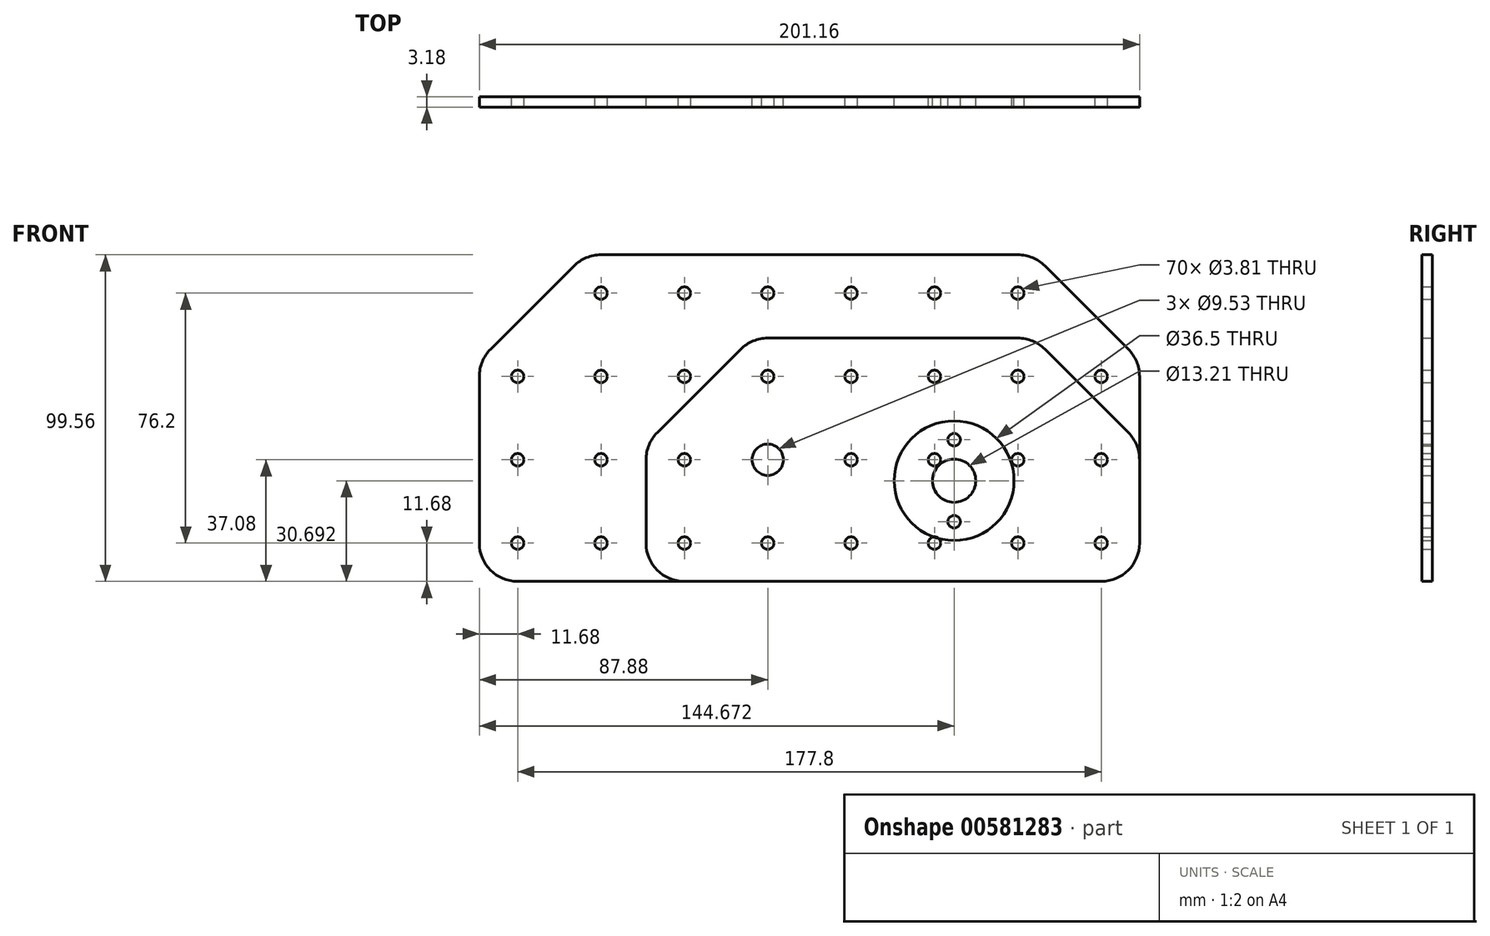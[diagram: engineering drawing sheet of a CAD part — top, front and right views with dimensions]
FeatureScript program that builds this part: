
annotation { "Feature Type Name" : "Feature", "Feature Type Description" : "" }
export const myFeature = defineFeature(function(context is Context, id is Id, definition is map)
    precondition{}
    {
        {
            var Q0;
            Q0=qCreatedBy(makeId("Front.planeOp"),FACE);
            var sketch = newSketch(context, id + "F0", { "sketchPlane" : qUnion([Q0])});
            skCircle(sketch, "E0", {"center": v(0, 0) * mm, "radius": 4.76 * mm});
            skCircle(sketch, "E1", {"center": v(0, 0) * mm, "radius": 50.8 * mm, "construction": true});
            skCircle(sketch, "E2", {"center": v(0, 0) * mm, "radius": 25.4 * mm, "construction": true});
            skCircle(sketch, "E3", {"center": v(56.8, -6.39) * mm, "radius": 6.6 * mm});
            skCircle(sketch, "E4", {"center": v(56.8, -6.39) * mm, "radius": 6.35 * mm, "construction": true});
            skCircle(sketch, "E5", {"center": v(56.8, -18.88) * mm, "radius": 1.9 * mm});
            skCircle(sketch, "E6", {"center": v(56.8, 6.1) * mm, "radius": 1.9 * mm});
            skLineSegment(sketch, "E7", {"start": v(56.8, -18.88) * mm, "end": v(56.8, 6.1) * mm, "construction": true});
            skCircle(sketch, "E8", {"center": v(56.8, -6.39) * mm, "radius": 18 * mm, "construction": true});
            skLineSegment(sketch, "E9", {"start": v(-87.88, -37.08) * mm, "end": v(113.28, -37.08) * mm});
            skCircle(sketch, "E10", {"center": v(0, 0) * mm, "radius": 6.35 * mm, "construction": true});
            skPoint(sketch, "E11", {"position": v(12.7, -37.08) * mm});
            skCircle(sketch, "E12", {"center": v(101.6, -25.4) * mm, "radius": 1.9 * mm});
            skCircle(sketch, "E13.0.1.0", {"center": v(101.6, 0) * mm, "radius": 1.9 * mm});
            skCircle(sketch, "E13.0.2.0", {"center": v(101.6, 25.4) * mm, "radius": 1.9 * mm});
            skCircle(sketch, "E13.0.3.0", {"center": v(101.6, 50.8) * mm, "radius": 1.9 * mm, "construction": true});
            skCircle(sketch, "E13.1.0.0", {"center": v(76.2, -25.4) * mm, "radius": 1.9 * mm});
            skCircle(sketch, "E13.1.1.0", {"center": v(76.2, 0) * mm, "radius": 1.9 * mm});
            skCircle(sketch, "E13.1.2.0", {"center": v(76.2, 25.4) * mm, "radius": 1.9 * mm});
            skCircle(sketch, "E13.1.3.0", {"center": v(76.2, 50.8) * mm, "radius": 1.9 * mm});
            skCircle(sketch, "E13.2.0.0", {"center": v(50.8, -25.4) * mm, "radius": 1.9 * mm, "construction": true});
            skCircle(sketch, "E13.2.1.0", {"center": v(50.8, 0) * mm, "radius": 1.9 * mm, "construction": true});
            skCircle(sketch, "E13.2.2.0", {"center": v(50.8, 25.4) * mm, "radius": 1.9 * mm});
            skCircle(sketch, "E13.2.3.0", {"center": v(50.8, 50.8) * mm, "radius": 1.9 * mm});
            skCircle(sketch, "E13.3.0.0", {"center": v(25.4, -25.4) * mm, "radius": 1.9 * mm});
            skCircle(sketch, "E13.3.1.0", {"center": v(25.4, 0) * mm, "radius": 1.9 * mm});
            skCircle(sketch, "E13.3.2.0", {"center": v(25.4, 25.4) * mm, "radius": 1.9 * mm});
            skCircle(sketch, "E13.3.3.0", {"center": v(25.4, 50.8) * mm, "radius": 1.9 * mm});
            skCircle(sketch, "E13.4.0.0", {"center": v(0, -25.4) * mm, "radius": 1.9 * mm});
            skCircle(sketch, "E13.4.1.0", {"center": v(0, 0) * mm, "radius": 1.9 * mm, "construction": true});
            skCircle(sketch, "E13.4.2.0", {"center": v(0, 25.4) * mm, "radius": 1.9 * mm});
            skCircle(sketch, "E13.4.3.0", {"center": v(0, 50.8) * mm, "radius": 1.9 * mm});
            skCircle(sketch, "E13.5.0.0", {"center": v(-25.4, -25.4) * mm, "radius": 1.9 * mm});
            skCircle(sketch, "E13.5.1.0", {"center": v(-25.4, 0) * mm, "radius": 1.9 * mm});
            skCircle(sketch, "E13.5.2.0", {"center": v(-25.4, 25.4) * mm, "radius": 1.9 * mm});
            skCircle(sketch, "E13.5.3.0", {"center": v(-25.4, 50.8) * mm, "radius": 1.9 * mm});
            skCircle(sketch, "E13.6.0.0", {"center": v(-50.8, -25.4) * mm, "radius": 1.9 * mm});
            skCircle(sketch, "E13.6.1.0", {"center": v(-50.8, 0) * mm, "radius": 1.9 * mm});
            skCircle(sketch, "E13.6.2.0", {"center": v(-50.8, 25.4) * mm, "radius": 1.9 * mm});
            skCircle(sketch, "E13.6.3.0", {"center": v(-50.8, 50.8) * mm, "radius": 1.9 * mm});
            skCircle(sketch, "E13.7.0.0", {"center": v(-76.2, -25.4) * mm, "radius": 1.9 * mm});
            skCircle(sketch, "E13.7.1.0", {"center": v(-76.2, 0) * mm, "radius": 1.9 * mm});
            skCircle(sketch, "E13.7.2.0", {"center": v(-76.2, 25.4) * mm, "radius": 1.9 * mm});
            skCircle(sketch, "E13.7.3.0", {"center": v(-76.2, 50.8) * mm, "radius": 1.9 * mm, "construction": true});
            skLineSegment(sketch, "E13.direction1", {"start": v(101.6, -25.4) * mm, "end": v(76.2, -25.4) * mm, "construction": true});
            skLineSegment(sketch, "E13.direction2", {"start": v(101.6, -25.4) * mm, "end": v(101.6, 0) * mm, "construction": true});
            skLineSegment(sketch, "E14", {"start": v(113.28, -37.08) * mm, "end": v(113.28, 30.24) * mm});
            skLineSegment(sketch, "E15", {"start": v(113.28, 30.24) * mm, "end": v(81.04, 62.48) * mm});
            skLineSegment(sketch, "E16", {"start": v(81.04, 62.48) * mm, "end": v(-55.64, 62.48) * mm});
            skLineSegment(sketch, "E17", {"start": v(-55.64, 62.48) * mm, "end": v(-87.88, 30.24) * mm});
            skLineSegment(sketch, "E18", {"start": v(-87.88, 30.24) * mm, "end": v(-87.88, -37.08) * mm});
            skPoint(sketch, "E19", {"position": v(12.7, 62.48) * mm});
            skSolve(sketch);
        }
        {
            var Q0;
            Q0 = qSketchRegion(id + "F0", true);
            extrude(context, id + "F1", {"entities" : qUnion([Q0]), "depth" : 3.17 * mm, "offsetDistance" : 25.4 * mm});
        }
        {
            var Q0;
            Q0=qCreatedBy(makeId("Front.planeOp"),FACE);
            var sketch = newSketch(context, id + "F2", { "sketchPlane" : qUnion([Q0])});
            skCircle(sketch, "E20", {"center": v(0, 0) * mm, "radius": 4.76 * mm});
            skCircle(sketch, "E21", {"center": v(0, 0) * mm, "radius": 50.8 * mm, "construction": true});
            skCircle(sketch, "E22", {"center": v(0, 0) * mm, "radius": 25.4 * mm, "construction": true});
            skCircle(sketch, "E23", {"center": v(56.8, -6.39) * mm, "radius": 6.6 * mm, "construction": true});
            skCircle(sketch, "E24", {"center": v(56.8, -6.39) * mm, "radius": 6.35 * mm, "construction": true});
            skCircle(sketch, "E25", {"center": v(56.8, -18.88) * mm, "radius": 1.9 * mm, "construction": true});
            skCircle(sketch, "E26", {"center": v(56.8, 6.1) * mm, "radius": 1.9 * mm, "construction": true});
            skLineSegment(sketch, "E27", {"start": v(56.8, -18.88) * mm, "end": v(56.8, 6.1) * mm, "construction": true});
            skCircle(sketch, "E28", {"center": v(56.8, -6.39) * mm, "radius": 18 * mm, "construction": true});
            skLineSegment(sketch, "E29", {"start": v(-87.88, -37.08) * mm, "end": v(113.28, -37.08) * mm});
            skCircle(sketch, "E30", {"center": v(0, 0) * mm, "radius": 6.35 * mm, "construction": true});
            skPoint(sketch, "E31", {"position": v(12.7, -37.08) * mm});
            skCircle(sketch, "E32", {"center": v(101.6, -25.4) * mm, "radius": 1.9 * mm});
            skCircle(sketch, "E33.0.1.0", {"center": v(101.6, 0) * mm, "radius": 1.9 * mm});
            skCircle(sketch, "E33.0.2.0", {"center": v(101.6, 25.4) * mm, "radius": 1.9 * mm});
            skCircle(sketch, "E33.0.3.0", {"center": v(101.6, 50.8) * mm, "radius": 1.9 * mm, "construction": true});
            skCircle(sketch, "E33.1.0.0", {"center": v(76.2, -25.4) * mm, "radius": 1.9 * mm});
            skCircle(sketch, "E33.1.1.0", {"center": v(76.2, 0) * mm, "radius": 1.9 * mm});
            skCircle(sketch, "E33.1.2.0", {"center": v(76.2, 25.4) * mm, "radius": 1.9 * mm});
            skCircle(sketch, "E33.1.3.0", {"center": v(76.2, 50.8) * mm, "radius": 1.9 * mm});
            skCircle(sketch, "E33.2.0.0", {"center": v(50.8, -25.4) * mm, "radius": 1.9 * mm});
            skCircle(sketch, "E33.2.1.0", {"center": v(50.8, 0) * mm, "radius": 1.9 * mm});
            skCircle(sketch, "E33.2.2.0", {"center": v(50.8, 25.4) * mm, "radius": 1.9 * mm});
            skCircle(sketch, "E33.2.3.0", {"center": v(50.8, 50.8) * mm, "radius": 1.9 * mm});
            skCircle(sketch, "E33.3.0.0", {"center": v(25.4, -25.4) * mm, "radius": 1.9 * mm});
            skCircle(sketch, "E33.3.1.0", {"center": v(25.4, 0) * mm, "radius": 1.9 * mm});
            skCircle(sketch, "E33.3.2.0", {"center": v(25.4, 25.4) * mm, "radius": 1.9 * mm});
            skCircle(sketch, "E33.3.3.0", {"center": v(25.4, 50.8) * mm, "radius": 1.9 * mm});
            skCircle(sketch, "E33.4.0.0", {"center": v(0, -25.4) * mm, "radius": 1.9 * mm});
            skCircle(sketch, "E33.4.1.0", {"center": v(0, 0) * mm, "radius": 1.9 * mm, "construction": true});
            skCircle(sketch, "E33.4.2.0", {"center": v(0, 25.4) * mm, "radius": 1.9 * mm});
            skCircle(sketch, "E33.4.3.0", {"center": v(0, 50.8) * mm, "radius": 1.9 * mm});
            skCircle(sketch, "E33.5.0.0", {"center": v(-25.4, -25.4) * mm, "radius": 1.9 * mm});
            skCircle(sketch, "E33.5.1.0", {"center": v(-25.4, 0) * mm, "radius": 1.9 * mm});
            skCircle(sketch, "E33.5.2.0", {"center": v(-25.4, 25.4) * mm, "radius": 1.9 * mm});
            skCircle(sketch, "E33.5.3.0", {"center": v(-25.4, 50.8) * mm, "radius": 1.9 * mm});
            skCircle(sketch, "E33.6.0.0", {"center": v(-50.8, -25.4) * mm, "radius": 1.9 * mm});
            skCircle(sketch, "E33.6.1.0", {"center": v(-50.8, 0) * mm, "radius": 1.9 * mm});
            skCircle(sketch, "E33.6.2.0", {"center": v(-50.8, 25.4) * mm, "radius": 1.9 * mm});
            skCircle(sketch, "E33.6.3.0", {"center": v(-50.8, 50.8) * mm, "radius": 1.9 * mm});
            skCircle(sketch, "E33.7.0.0", {"center": v(-76.2, -25.4) * mm, "radius": 1.9 * mm});
            skCircle(sketch, "E33.7.1.0", {"center": v(-76.2, 0) * mm, "radius": 1.9 * mm});
            skCircle(sketch, "E33.7.2.0", {"center": v(-76.2, 25.4) * mm, "radius": 1.9 * mm});
            skCircle(sketch, "E33.7.3.0", {"center": v(-76.2, 50.8) * mm, "radius": 1.9 * mm, "construction": true});
            skLineSegment(sketch, "E33.direction1", {"start": v(101.6, -25.4) * mm, "end": v(76.2, -25.4) * mm, "construction": true});
            skLineSegment(sketch, "E33.direction2", {"start": v(101.6, -25.4) * mm, "end": v(101.6, 0) * mm, "construction": true});
            skLineSegment(sketch, "E34", {"start": v(113.28, -37.08) * mm, "end": v(113.28, 30.24) * mm});
            skLineSegment(sketch, "E35", {"start": v(113.28, 30.24) * mm, "end": v(81.04, 62.48) * mm});
            skLineSegment(sketch, "E36", {"start": v(81.04, 62.48) * mm, "end": v(-55.64, 62.48) * mm});
            skLineSegment(sketch, "E37", {"start": v(-55.64, 62.48) * mm, "end": v(-87.88, 30.24) * mm});
            skLineSegment(sketch, "E38", {"start": v(-87.88, 30.24) * mm, "end": v(-87.88, -37.08) * mm});
            skPoint(sketch, "E39", {"position": v(12.7, 62.48) * mm});
            skSolve(sketch);
        }
        {
            var Q0;
            Q0 = qSketchRegion(id + "F2", true);
            extrude(context, id + "F3", {"entities" : qUnion([Q0]), "depth" : 3.17 * mm, "offsetDistance" : 25.4 * mm});
        }
        {
            var Q0;
            Q0=qCreatedBy(makeId("Front.planeOp"),FACE);
            var sketch = newSketch(context, id + "F4", { "sketchPlane" : qUnion([Q0])});
            skLineSegment(sketch, "E40.0", {"start": v(-87.88, -37.08) * mm, "end": v(113.28, -37.08) * mm, "construction": true});
            skCircle(sketch, "E40.1", {"center": v(101.6, -25.4) * mm, "radius": 1.9 * mm});
            skCircle(sketch, "E40.2", {"center": v(76.2, -25.4) * mm, "radius": 1.9 * mm});
            skCircle(sketch, "E40.3", {"center": v(50.8, -25.4) * mm, "radius": 1.9 * mm, "construction": true});
            skCircle(sketch, "E40.4", {"center": v(25.4, -25.4) * mm, "radius": 1.9 * mm});
            skCircle(sketch, "E40.5", {"center": v(25.4, 0) * mm, "radius": 1.9 * mm});
            skCircle(sketch, "E40.6", {"center": v(50.8, 25.4) * mm, "radius": 1.9 * mm});
            skCircle(sketch, "E40.7", {"center": v(76.2, 25.4) * mm, "radius": 1.9 * mm});
            skCircle(sketch, "E40.8", {"center": v(101.6, 0) * mm, "radius": 1.9 * mm});
            skCircle(sketch, "E40.9", {"center": v(76.2, 0) * mm, "radius": 1.9 * mm, "construction": true});
            skCircle(sketch, "E40.10", {"center": v(50.8, 0) * mm, "radius": 1.9 * mm, "construction": true});
            skLineSegment(sketch, "E40.11", {"start": v(113.28, -37.08) * mm, "end": v(113.28, 30.24) * mm, "construction": true});
            skCircle(sketch, "E41.0", {"center": v(56.8, -6.39) * mm, "radius": 18 * mm, "construction": true});
            skCircle(sketch, "E42.0", {"center": v(0, 0) * mm, "radius": 4.76 * mm});
            skCircle(sketch, "E43.0", {"center": v(0, -25.4) * mm, "radius": 1.9 * mm});
            skCircle(sketch, "E43.1", {"center": v(-25.4, -25.4) * mm, "radius": 1.9 * mm});
            skCircle(sketch, "E43.2", {"center": v(-25.4, 0) * mm, "radius": 1.9 * mm});
            skCircle(sketch, "E43.3", {"center": v(-25.4, 25.4) * mm, "radius": 1.9 * mm, "construction": true});
            skCircle(sketch, "E43.4", {"center": v(0, 25.4) * mm, "radius": 1.9 * mm});
            skCircle(sketch, "E43.5", {"center": v(25.4, 25.4) * mm, "radius": 1.9 * mm});
            skCircle(sketch, "E43.6", {"center": v(101.6, 25.4) * mm, "radius": 1.9 * mm, "construction": true});
            skCircle(sketch, "E44", {"center": v(56.8, -6.39) * mm, "radius": 18.25 * mm});
            skLineSegment(sketch, "E45", {"start": v(-37.08, -37.08) * mm, "end": v(-37.08, 4.84) * mm});
            skLineSegment(sketch, "E46", {"start": v(-37.08, 4.84) * mm, "end": v(-4.84, 37.08) * mm});
            skLineSegment(sketch, "E47", {"start": v(-4.84, 37.08) * mm, "end": v(81.04, 37.08) * mm});
            skLineSegment(sketch, "E48", {"start": v(81.04, 37.08) * mm, "end": v(113.28, 4.84) * mm});
            skLineSegment(sketch, "E49", {"start": v(113.28, 4.84) * mm, "end": v(113.28, -37.08) * mm});
            skLineSegment(sketch, "E50", {"start": v(113.28, -37.08) * mm, "end": v(-37.08, -37.08) * mm});
            skLineSegment(sketch, "E51", {"start": v(-25.4, 0) * mm, "end": v(0, 25.4) * mm, "construction": true});
            skLineSegment(sketch, "E52", {"start": v(76.2, 25.4) * mm, "end": v(101.6, 0) * mm, "construction": true});
            skSolve(sketch);
        }
        {
            var Q0;
            Q0 = qSketchRegion(id + "F4", true);
            extrude(context, id + "F5", {"entities" : qUnion([Q0]), "depth" : 3.17 * mm, "offsetDistance" : 25.4 * mm});
        }
        {
            var Q0;
            Q0=makeQuery(id+"F1.opExtrude","SWEPT_EDGE",EDGE,{"disambiguationData":[OSD([sQuery(id+"F0.wireOp",EDGE,"F7AttZYQ-Yins-SvBP-Eppq-Xn4QXeFlinCJ"),sQuery(id+"F0.wireOp",EDGE,"6gPZtXe4-BoHf-aHIe-cOLa-666qjqNs6mSt")])]});
            var Q1;
            Q1=makeQuery(id+"F1.opExtrude","SWEPT_EDGE",EDGE,{"disambiguationData":[OSD([sQuery(id+"F0.wireOp",EDGE,"6gPZtXe4-BoHf-aHIe-cOLa-666qjqNs6mSt"),sQuery(id+"F0.wireOp",EDGE,"hPgCTbiv-x1Vt-jTF2-6eVE-KaycVLD48by9")])]});
            var Q2;
            Q2=makeQuery(id+"F1.opExtrude","SWEPT_EDGE",EDGE,{"disambiguationData":[OSD([sQuery(id+"F0.wireOp",EDGE,"hPgCTbiv-x1Vt-jTF2-6eVE-KaycVLD48by9"),sQuery(id+"F0.wireOp",EDGE,"779TURws-2tXc-dS5s-yWGt-WtRSWQi4IZOo")])]});
            var Q3;
            Q3=makeQuery(id+"F1.opExtrude","SWEPT_EDGE",EDGE,{"disambiguationData":[OSD([sQuery(id+"F0.wireOp",EDGE,"3ukzmnzP-7FHP-AVdg-hM9W-DiS82MNKaoO8"),sQuery(id+"F0.wireOp",EDGE,"779TURws-2tXc-dS5s-yWGt-WtRSWQi4IZOo")])]});
            var Q4;
            Q4=makeQuery(id+"F1.opExtrude","SWEPT_EDGE",EDGE,{"disambiguationData":[OSD([sQuery(id+"F0.wireOp",EDGE,"E9"),sQuery(id+"F0.wireOp",EDGE,"3ukzmnzP-7FHP-AVdg-hM9W-DiS82MNKaoO8")])]});
            var Q5;
            Q5=makeQuery(id+"F1.opExtrude","SWEPT_EDGE",EDGE,{"disambiguationData":[OSD([sQuery(id+"F0.wireOp",EDGE,"E9"),sQuery(id+"F0.wireOp",EDGE,"F7AttZYQ-Yins-SvBP-Eppq-Xn4QXeFlinCJ")])]});
            var Q6;
            Q6=makeQuery(id+"F3.opExtrude","SWEPT_EDGE",EDGE,{"disambiguationData":[OSD([sQuery(id+"F0.wireOp",EDGE,"F7AttZYQ-Yins-SvBP-Eppq-Xn4QXeFlinCJ"),sQuery(id+"F0.wireOp",EDGE,"6gPZtXe4-BoHf-aHIe-cOLa-666qjqNs6mSt")])]});
            var Q7;
            Q7=makeQuery(id+"F3.opExtrude","SWEPT_EDGE",EDGE,{"disambiguationData":[OSD([sQuery(id+"F0.wireOp",EDGE,"6gPZtXe4-BoHf-aHIe-cOLa-666qjqNs6mSt"),sQuery(id+"F0.wireOp",EDGE,"hPgCTbiv-x1Vt-jTF2-6eVE-KaycVLD48by9")])]});
            var Q8;
            Q8=makeQuery(id+"F3.opExtrude","SWEPT_EDGE",EDGE,{"disambiguationData":[OSD([sQuery(id+"F0.wireOp",EDGE,"hPgCTbiv-x1Vt-jTF2-6eVE-KaycVLD48by9"),sQuery(id+"F0.wireOp",EDGE,"779TURws-2tXc-dS5s-yWGt-WtRSWQi4IZOo")])]});
            var Q9;
            Q9=makeQuery(id+"F3.opExtrude","SWEPT_EDGE",EDGE,{"disambiguationData":[OSD([sQuery(id+"F0.wireOp",EDGE,"3ukzmnzP-7FHP-AVdg-hM9W-DiS82MNKaoO8"),sQuery(id+"F0.wireOp",EDGE,"779TURws-2tXc-dS5s-yWGt-WtRSWQi4IZOo")])]});
            var Q10;
            Q10=makeQuery(id+"F3.opExtrude","SWEPT_EDGE",EDGE,{"disambiguationData":[OSD([sQuery(id+"F0.wireOp",EDGE,"E9"),sQuery(id+"F0.wireOp",EDGE,"3ukzmnzP-7FHP-AVdg-hM9W-DiS82MNKaoO8")])]});
            var Q11;
            Q11=makeQuery(id+"F3.opExtrude","SWEPT_EDGE",EDGE,{"disambiguationData":[OSD([sQuery(id+"F0.wireOp",EDGE,"E9"),sQuery(id+"F0.wireOp",EDGE,"F7AttZYQ-Yins-SvBP-Eppq-Xn4QXeFlinCJ")])]});
            var Q12;
            Q12=makeQuery(id+"F5.opExtrude","SWEPT_EDGE",EDGE,{"disambiguationData":[OSD([sQuery(id+"F4.wireOp",EDGE,"TzD5XU4E-TGGQ-1EQO-ZL9j-mCSe5aHl6gHs"),sQuery(id+"F4.wireOp",EDGE,"8n2z0Ezk-yPWO-kxb6-UokY-uYDiX3D4AePN")])]});
            var Q13;
            Q13=makeQuery(id+"F5.opExtrude","SWEPT_EDGE",EDGE,{"disambiguationData":[OSD([sQuery(id+"F4.wireOp",EDGE,"8n2z0Ezk-yPWO-kxb6-UokY-uYDiX3D4AePN"),sQuery(id+"F4.wireOp",EDGE,"KczUjEY5-OVIH-cB5R-5asA-Ua5ha0n8nFp0")])]});
            var Q14;
            Q14=makeQuery(id+"F5.opExtrude","SWEPT_EDGE",EDGE,{"disambiguationData":[OSD([sQuery(id+"F4.wireOp",EDGE,"KczUjEY5-OVIH-cB5R-5asA-Ua5ha0n8nFp0"),sQuery(id+"F4.wireOp",EDGE,"vwqXhOkg-Ff4W-U12V-nxzQ-0fkIC5sZluZW")])]});
            var Q15;
            Q15=makeQuery(id+"F5.opExtrude","SWEPT_EDGE",EDGE,{"disambiguationData":[OSD([sQuery(id+"F4.wireOp",EDGE,"9ce8081b-72da-4d30-9341-2ed91e038d45.3"),sQuery(id+"F4.wireOp",EDGE,"vwqXhOkg-Ff4W-U12V-nxzQ-0fkIC5sZluZW")])]});
            var Q16;
            Q16=makeQuery(id+"F5.opExtrude","SWEPT_EDGE",EDGE,{"disambiguationData":[OSD([sQuery(id+"F4.wireOp",EDGE,"9ce8081b-72da-4d30-9341-2ed91e038d45.3"),sQuery(id+"F4.wireOp",EDGE,"9ce8081b-72da-4d30-9341-2ed91e038d45.4")])]});
            var Q17;
            Q17=makeQuery(id+"F5.opExtrude","SWEPT_EDGE",EDGE,{"disambiguationData":[OSD([sQuery(id+"F4.wireOp",EDGE,"9ce8081b-72da-4d30-9341-2ed91e038d45.4"),sQuery(id+"F4.wireOp",EDGE,"TzD5XU4E-TGGQ-1EQO-ZL9j-mCSe5aHl6gHs")])]});
            var Q18;
            Q18=makeQuery(id+"F5.opExtrude","SWEPT_EDGE",EDGE,{"disambiguationData":[OSD([sQuery(id+"F4.wireOp",EDGE,"E45"),sQuery(id+"F4.wireOp",EDGE,"E50")])]});
            var Q19;
            Q19=makeQuery(id+"F5.opExtrude","SWEPT_EDGE",EDGE,{"disambiguationData":[OSD([sQuery(id+"F4.wireOp",EDGE,"E45"),sQuery(id+"F4.wireOp",EDGE,"E46")])]});
            var Q20;
            Q20=makeQuery(id+"F5.opExtrude","SWEPT_EDGE",EDGE,{"disambiguationData":[OSD([sQuery(id+"F4.wireOp",EDGE,"E46"),sQuery(id+"F4.wireOp",EDGE,"E47")])]});
            var Q21;
            Q21=makeQuery(id+"F5.opExtrude","SWEPT_EDGE",EDGE,{"disambiguationData":[OSD([sQuery(id+"F4.wireOp",EDGE,"E47"),sQuery(id+"F4.wireOp",EDGE,"E48")])]});
            var Q22;
            Q22=makeQuery(id+"F5.opExtrude","SWEPT_EDGE",EDGE,{"disambiguationData":[OSD([sQuery(id+"F4.wireOp",EDGE,"E48"),sQuery(id+"F4.wireOp",EDGE,"E49")])]});
            var Q23;
            Q23=makeQuery(id+"F5.opExtrude","SWEPT_EDGE",EDGE,{"disambiguationData":[OSD([sQuery(id+"F4.wireOp",EDGE,"E49"),sQuery(id+"F4.wireOp",EDGE,"E50")])]});
            var Q24;
            Q24=makeQuery(id+"F3.opExtrude","SWEPT_EDGE",EDGE,{"disambiguationData":[OSD([sQuery(id+"F2.wireOp",EDGE,"E29"),sQuery(id+"F2.wireOp",EDGE,"E38")])]});
            var Q25;
            Q25=makeQuery(id+"F3.opExtrude","SWEPT_EDGE",EDGE,{"disambiguationData":[OSD([sQuery(id+"F2.wireOp",EDGE,"E37"),sQuery(id+"F2.wireOp",EDGE,"E38")])]});
            var Q26;
            Q26=makeQuery(id+"F3.opExtrude","SWEPT_EDGE",EDGE,{"disambiguationData":[OSD([sQuery(id+"F2.wireOp",EDGE,"E36"),sQuery(id+"F2.wireOp",EDGE,"E37")])]});
            var Q27;
            Q27=makeQuery(id+"F3.opExtrude","SWEPT_EDGE",EDGE,{"disambiguationData":[OSD([sQuery(id+"F2.wireOp",EDGE,"E35"),sQuery(id+"F2.wireOp",EDGE,"E36")])]});
            var Q28;
            Q28=makeQuery(id+"F3.opExtrude","SWEPT_EDGE",EDGE,{"disambiguationData":[OSD([sQuery(id+"F2.wireOp",EDGE,"E34"),sQuery(id+"F2.wireOp",EDGE,"E35")])]});
            var Q29;
            Q29=makeQuery(id+"F3.opExtrude","SWEPT_EDGE",EDGE,{"disambiguationData":[OSD([sQuery(id+"F2.wireOp",EDGE,"E29"),sQuery(id+"F2.wireOp",EDGE,"E34")])]});
            var Q30;
            Q30=makeQuery(id+"F1.opExtrude","SWEPT_EDGE",EDGE,{"disambiguationData":[OSD([sQuery(id+"F0.wireOp",EDGE,"E14"),sQuery(id+"F0.wireOp",EDGE,"E15")])]});
            var Q31;
            Q31=makeQuery(id+"F1.opExtrude","SWEPT_EDGE",EDGE,{"disambiguationData":[OSD([sQuery(id+"F0.wireOp",EDGE,"E15"),sQuery(id+"F0.wireOp",EDGE,"E16")])]});
            var Q32;
            Q32=makeQuery(id+"F1.opExtrude","SWEPT_EDGE",EDGE,{"disambiguationData":[OSD([sQuery(id+"F0.wireOp",EDGE,"E16"),sQuery(id+"F0.wireOp",EDGE,"E17")])]});
            var Q33;
            Q33=makeQuery(id+"F1.opExtrude","SWEPT_EDGE",EDGE,{"disambiguationData":[OSD([sQuery(id+"F0.wireOp",EDGE,"E17"),sQuery(id+"F0.wireOp",EDGE,"E18")])]});
            fillet(context, id + "F6", {"entities" : qUnion([Q0, Q1, Q2, Q3, Q4, Q5, Q6, Q7, Q8, Q9, Q10, Q11, Q12, Q13, Q14, Q15, Q16, Q17, Q18, Q19, Q20, Q21, Q22, Q23, Q24, Q25, Q26, Q27, Q28, Q29, Q30, Q31, Q32, Q33]), "radius" : 11.68 * mm, "tangentPropagation" : true, "allowEdgeOverflow" : false});
        }
    });
